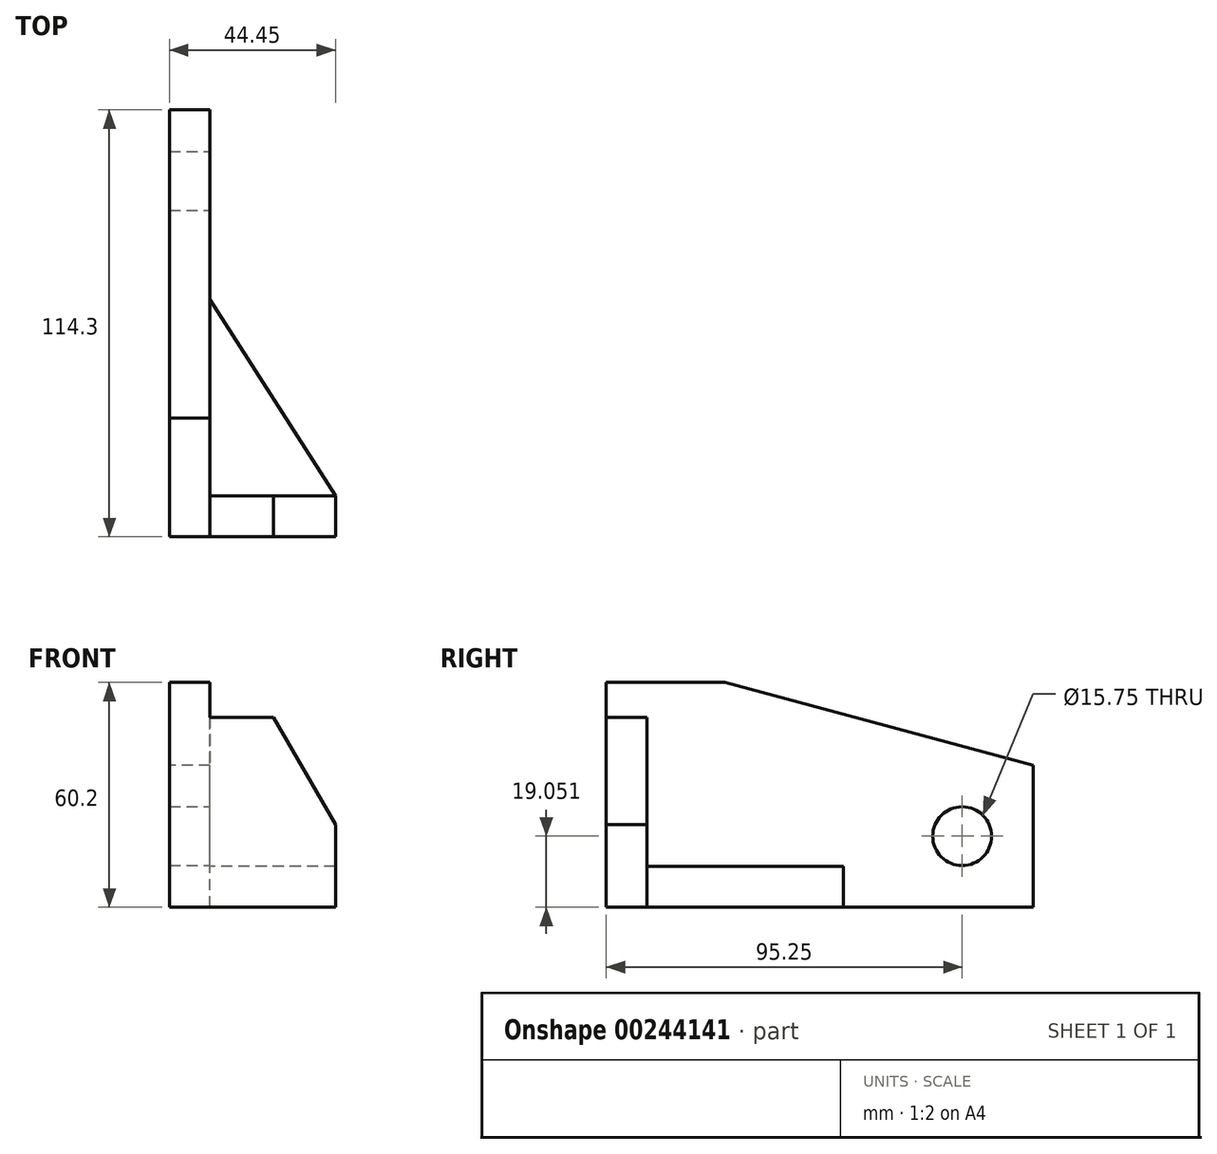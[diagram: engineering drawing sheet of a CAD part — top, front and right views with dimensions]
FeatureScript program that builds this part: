
annotation { "Feature Type Name" : "Feature", "Feature Type Description" : "" }
export const myFeature = defineFeature(function(context is Context, id is Id, definition is map)
    precondition{}
    {
        {
            var Q0;
            Q0=qCreatedBy(makeId("Front.planeOp"),FACE);
            var sketch = newSketch(context, id + "F0", { "sketchPlane" : qUnion([Q0])});
            skLineSegment(sketch, "E0.bottom", {"start": v(5.46, -30.1) * mm, "end": v(-5.46, -30.1) * mm});
            skLineSegment(sketch, "E0.top", {"start": v(5.46, 30.1) * mm, "end": v(-5.46, 30.1) * mm});
            skLineSegment(sketch, "E0.left", {"start": v(5.46, -30.1) * mm, "end": v(5.46, 30.1) * mm});
            skLineSegment(sketch, "E0.right", {"start": v(-5.46, -30.1) * mm, "end": v(-5.46, 30.1) * mm});
            skPoint(sketch, "E0.middle", {"position": v(0, 0) * mm});
            skSolve(sketch);
        }
        {
            var Q0;
            Q0 = qSketchRegion(id + "F0", true);
            extrude(context, id + "F1", {"entities" : qUnion([Q0]), "depth" : 114.3 * mm});
        }
        {
            var Q0;
            Q0=makeQuery(id+"F1.opExtrude","SWEPT_FACE",FACE,{"disambiguationData":[OSD([sQuery(id+"F0.wireOp",EDGE,"E0.right")])]});
            var sketch = newSketch(context, id + "F2", { "sketchPlane" : qUnion([Q0])});
            skLineSegment(sketch, "E1", {"start": v(114.3, 30.1) * mm, "end": v(82.55, 30.1) * mm});
            skLineSegment(sketch, "E2", {"start": v(82.55, 30.1) * mm, "end": v(0, 7.98) * mm});
            skSolve(sketch);
        }
        {
            var Q0;
            {var subQ0=sQuery(id+"F2.wireOp",EDGE,"E2");Q0=makeQuery(id+"F2.imprint","IMPRINT",FACE,{"disambiguationData":[TD([[makeQuery(id+"F2.imprint","IMPRINT",EDGE,{"derivedFrom":subQ0}),-1.0]])]});}
            extrude(context, id + "F3", {"entities" : qUnion([Q0]), "operationType" : NewBodyOperationType.REMOVE, "oppositeDirection" : true, "depth" : 10.92 * mm});
        }
        {
            var Q0;
            Q0=makeQuery(id+"F1.opExtrude","SWEPT_FACE",FACE,{"disambiguationData":[OSD([sQuery(id+"F0.wireOp",EDGE,"E0.left")])]});
            var sketch = newSketch(context, id + "F4", { "sketchPlane" : qUnion([Q0])});
            skLineSegment(sketch, "E3.bottom", {"start": v(-114.3, -30.1) * mm, "end": v(-103.38, -30.1) * mm});
            skLineSegment(sketch, "E3.top", {"start": v(-114.3, 20.7) * mm, "end": v(-103.38, 20.7) * mm});
            skLineSegment(sketch, "E3.left", {"start": v(-114.3, -30.1) * mm, "end": v(-114.3, 20.7) * mm});
            skLineSegment(sketch, "E3.right", {"start": v(-103.38, -30.1) * mm, "end": v(-103.38, 20.7) * mm});
            skSolve(sketch);
        }
        {
            var Q0;
            Q0=makeQuery(id+"F4.imprint","IMPRINT",FACE,{"disambiguationData":[TD([[makeQuery(id+"F4.imprint","IMPRINT",EDGE,{"derivedFrom":sQuery(id+"F4.wireOp",EDGE,"E3.bottom")}),1.0]])]});
            extrude(context, id + "F5", {"entities" : qUnion([Q0]), "operationType" : NewBodyOperationType.ADD, "depth" : 33.53 * mm});
        }
        {
            var Q0;
            Q0=makeQuery(id+"F5.boolean.opBoolean","MERGE",FACE,{"derivedFrom":[makeQuery(id+"F1.opExtrude","CAP_FACE",FACE,{"disambiguationData":[OSD([sQuery(id+"F0.wireOp",EDGE,"E0.bottom"),sQuery(id+"F0.wireOp",EDGE,"E0.top"),sQuery(id+"F0.wireOp",EDGE,"E0.left"),sQuery(id+"F0.wireOp",EDGE,"E0.right")])],"isStart":false}),makeQuery(id+"F5.opExtrude","SWEPT_FACE",FACE,{"disambiguationData":[OSD([sQuery(id+"F4.wireOp",EDGE,"E3.left")])]})]});
            var sketch = newSketch(context, id + "F6", { "sketchPlane" : qUnion([Q0])});
            skLineSegment(sketch, "E4", {"start": v(38.99, -30.1) * mm, "end": v(38.99, -8) * mm});
            skLineSegment(sketch, "E5", {"start": v(38.99, -8) * mm, "end": v(22.42, 20.7) * mm});
            skLineSegment(sketch, "E6", {"start": v(38.99, -8) * mm, "end": v(5.36, -8) * mm, "construction": true});
            skSolve(sketch);
        }
        {
            var Q0;
            Q0 = qSketchRegion(id + "F6", true);
            var Q1;
            {var subQ0=sQuery(id+"F6.wireOp",EDGE,"E5");Q1=makeQuery(id+"F6.imprint","IMPRINT",FACE,{"disambiguationData":[TD([[makeQuery(id+"F6.imprint","IMPRINT",EDGE,{"derivedFrom":subQ0}),-1.0]])]});}
            extrude(context, id + "F7", {"entities" : qUnion([Q0, Q1]), "operationType" : NewBodyOperationType.REMOVE, "oppositeDirection" : true, "depth" : 10.92 * mm});
        }
        {
            var Q0;
            Q0=makeQuery(id+"F1.opExtrude","SWEPT_FACE",FACE,{"disambiguationData":[OSD([sQuery(id+"F0.wireOp",EDGE,"E0.left")])]});
            var sketch = newSketch(context, id + "F8", { "sketchPlane" : qUnion([Q0])});
            skLineSegment(sketch, "E7.bottom", {"start": v(-103.38, -30.1) * mm, "end": v(-50.8, -30.1) * mm});
            skLineSegment(sketch, "E7.top", {"start": v(-103.38, -19.18) * mm, "end": v(-50.8, -19.18) * mm});
            skLineSegment(sketch, "E7.left", {"start": v(-103.38, -30.1) * mm, "end": v(-103.38, -19.18) * mm});
            skLineSegment(sketch, "E7.right", {"start": v(-50.8, -30.1) * mm, "end": v(-50.8, -19.18) * mm});
            skSolve(sketch);
        }
        {
            var Q0;
            Q0 = qSketchRegion(id + "F8", true);
            var Q1;
            Q1 = qSketchRegion(id + "F6", true);
            extrude(context, id + "F9", {"entities" : qUnion([Q0, Q1]), "operationType" : NewBodyOperationType.ADD, "depth" : 33.53 * mm});
        }
        {
            var Q0;
            Q0=makeQuery(id+"F9.opExtrude","SWEPT_FACE",FACE,{"disambiguationData":[OSD([sQuery(id+"F8.wireOp",EDGE,"E7.top")])]});
            var sketch = newSketch(context, id + "F10", { "sketchPlane" : qUnion([Q0])});
            skLineSegment(sketch, "E8", {"start": v(38.99, -103.38) * mm, "end": v(5.46, -50.8) * mm});
            skLineSegment(sketch, "E9", {"start": v(5.46, -50.8) * mm, "end": v(38.99, -50.8) * mm});
            skLineSegment(sketch, "E10", {"start": v(38.99, -50.8) * mm, "end": v(38.99, -100.25) * mm});
            skLineSegment(sketch, "E11", {"start": v(38.99, -100.25) * mm, "end": v(38.99, -103.38) * mm});
            skSolve(sketch);
        }
        {
            var Q0;
            Q0=makeQuery(id+"F10.imprint","IMPRINT",FACE,{"disambiguationData":[TD([[makeQuery(id+"F10.imprint","IMPRINT",EDGE,{"derivedFrom":sQuery(id+"F10.wireOp",EDGE,"E8")}),-1.0]])]});
            extrude(context, id + "F11", {"entities" : qUnion([Q0]), "operationType" : NewBodyOperationType.REMOVE, "oppositeDirection" : true, "depth" : 10.92 * mm});
        }
        {
            var Q0;
            Q0=makeQuery(id+"F1.opExtrude","SWEPT_FACE",FACE,{"disambiguationData":[OSD([sQuery(id+"F0.wireOp",EDGE,"E0.left")])]});
            var sketch = newSketch(context, id + "F12", { "sketchPlane" : qUnion([Q0])});
            skLineSegment(sketch, "E12.bottom", {"start": v(0, -30.1) * mm, "end": v(-19.05, -30.1) * mm});
            skLineSegment(sketch, "E12.top", {"start": v(0, -11.05) * mm, "end": v(-11.18, -11.05) * mm});
            skLineSegment(sketch, "E12.left", {"start": v(0, -30.1) * mm, "end": v(0, -11.05) * mm});
            skLineSegment(sketch, "E12.right", {"start": v(-19.05, -30.1) * mm, "end": v(-19.05, -18.92) * mm});
            skCircle(sketch, "E13", {"center": v(-19.05, -11.05) * mm, "radius": 7.87 * mm});
            skSolve(sketch);
        }
        {
            var Q0;
            {var subQ0=sQuery(id+"F12.wireOp",EDGE,"E13");var subQ1=makeQuery(id+"F12.imprint","INTERSECT",VERTEX,{"derivedFrom":[sQuery(id+"F12.wireOp",EDGE,"E12.top"),subQ0]});Q0=makeQuery(id+"F12.imprint","IMPRINT",FACE,{"disambiguationData":[TD([[makeQuery(id+"F12.imprint","IMPRINT",EDGE,{"disambiguationData":[TD([[subQ1,-1.0]])],"derivedFrom":subQ0}),1.0]])]});}
            extrude(context, id + "F13", {"entities" : qUnion([Q0]), "operationType" : NewBodyOperationType.REMOVE, "oppositeDirection" : true, "depth" : 10.92 * mm});
        }
    });
